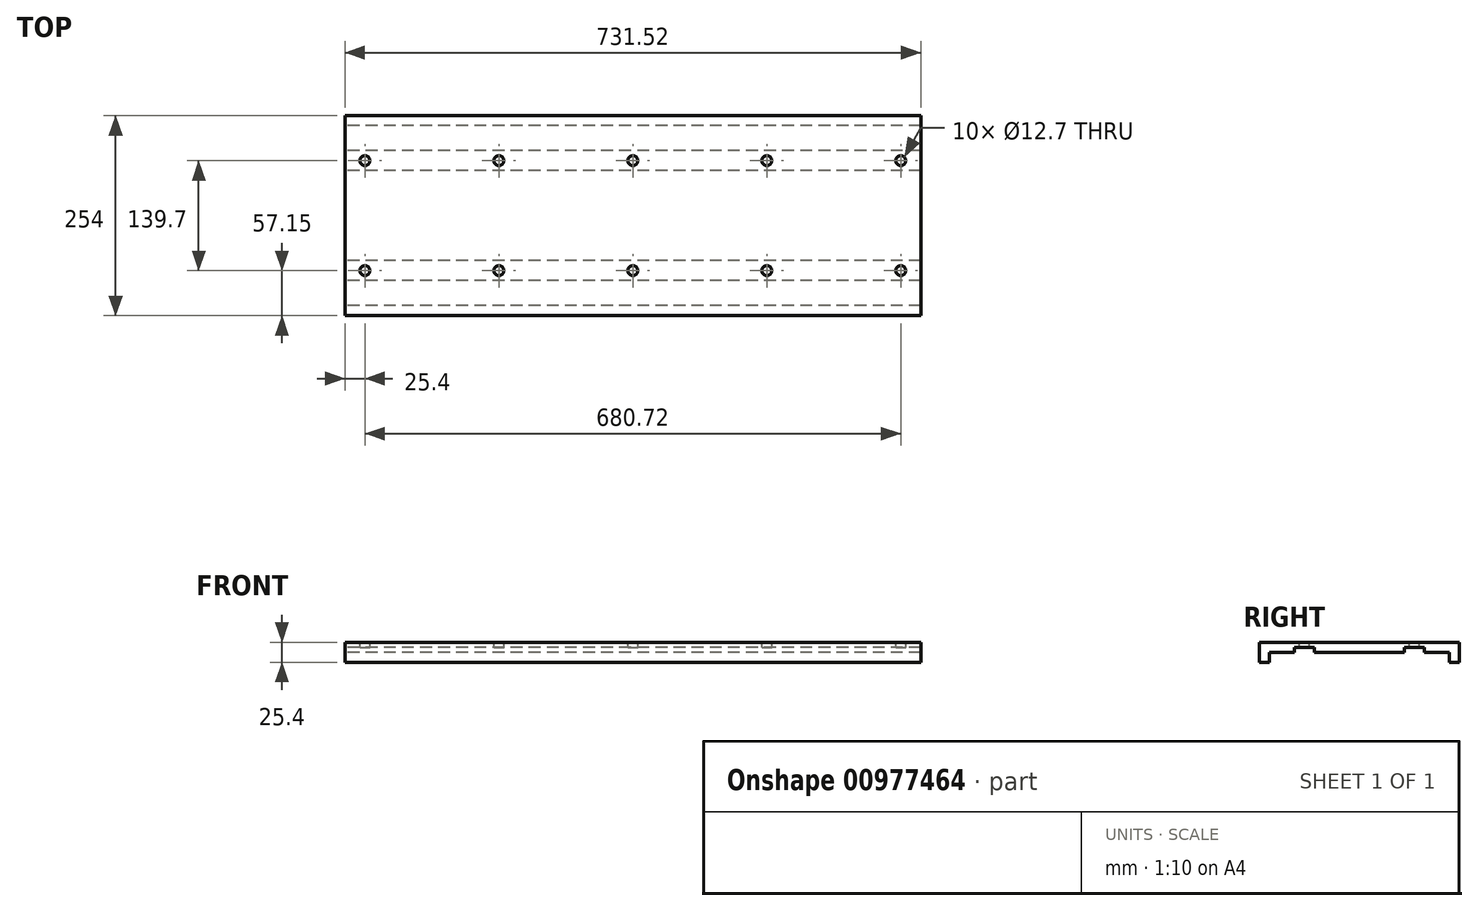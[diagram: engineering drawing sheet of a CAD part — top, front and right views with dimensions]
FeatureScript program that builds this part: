
annotation { "Feature Type Name" : "Feature", "Feature Type Description" : "" }
export const myFeature = defineFeature(function(context is Context, id is Id, definition is map)
    precondition{}
    {
        {
            var Q0;
            Q0=qCreatedBy(makeId("Right.planeOp"),FACE);
            var sketch = newSketch(context, id + "F0", { "sketchPlane" : qUnion([Q0])});
            skLineSegment(sketch, "E0.bottom", {"start": v(57.15, 6.35) * mm, "end": v(-57.15, 6.35) * mm});
            skLineSegment(sketch, "E0.top", {"start": v(57.15, -6.35) * mm, "end": v(-57.15, -6.35) * mm});
            skPoint(sketch, "E0.middle", {"position": v(0, 0) * mm});
            skLineSegment(sketch, "E1", {"start": v(-57.15, -6.35) * mm, "end": v(-57.15, 0) * mm});
            skLineSegment(sketch, "E2", {"start": v(-57.15, 0) * mm, "end": v(-82.55, 0) * mm});
            skLineSegment(sketch, "E3", {"start": v(-82.55, 0) * mm, "end": v(-82.55, -6.35) * mm});
            skLineSegment(sketch, "E4", {"start": v(-82.55, -6.35) * mm, "end": v(-114.3, -6.35) * mm});
            skLineSegment(sketch, "E5", {"start": v(-114.3, -6.35) * mm, "end": v(-114.3, -19.05) * mm});
            skLineSegment(sketch, "E6", {"start": v(-114.3, -19.05) * mm, "end": v(-127, -19.05) * mm});
            skLineSegment(sketch, "E7", {"start": v(-127, -19.05) * mm, "end": v(-127, 6.35) * mm});
            skLineSegment(sketch, "E8", {"start": v(-127, 6.35) * mm, "end": v(-57.15, 6.35) * mm});
            skLineSegment(sketch, "E9.MirrorCS", {"start": v(127, 6.35) * mm, "end": v(57.15, 6.35) * mm});
            skLineSegment(sketch, "E10.MirrorCS", {"start": v(127, -19.05) * mm, "end": v(127, 6.35) * mm});
            skLineSegment(sketch, "E11.MirrorCS", {"start": v(114.3, -19.05) * mm, "end": v(127, -19.05) * mm});
            skLineSegment(sketch, "E12.MirrorCS", {"start": v(82.55, -6.35) * mm, "end": v(114.3, -6.35) * mm});
            skLineSegment(sketch, "E13.MirrorCS", {"start": v(82.55, 0) * mm, "end": v(82.55, -6.35) * mm});
            skLineSegment(sketch, "E14.MirrorCS", {"start": v(57.15, 0) * mm, "end": v(82.55, 0) * mm});
            skLineSegment(sketch, "E15.MirrorCS", {"start": v(114.3, -6.35) * mm, "end": v(114.3, -19.05) * mm});
            skLineSegment(sketch, "E16.MirrorCS", {"start": v(57.15, -6.35) * mm, "end": v(57.15, 0) * mm});
            skSolve(sketch);
        }
        {
            var Q0;
            Q0=makeQuery(id+"F0.imprint","IMPRINT",FACE,{"disambiguationData":[TD([[makeQuery(id+"F0.imprint","IMPRINT",EDGE,{"derivedFrom":sQuery(id+"F0.wireOp",EDGE,"E0.bottom")}),1.0]])]});
            extrude(context, id + "F1", {"entities" : qUnion([Q0]), "endBound" : BoundingType.SYMMETRIC, "depth" : 731.52 * mm, "offsetDistance" : 25.4 * mm});
        }
        {
            var Q0;
            Q0=makeQuery(id+"F1.opExtrude","SWEPT_FACE",FACE,{"disambiguationData":[OSD([sQuery(id+"F0.wireOp",EDGE,"E0.bottom"),sQuery(id+"F0.wireOp",EDGE,"E8"),sQuery(id+"F0.wireOp",EDGE,"E9.MirrorCS")])]});
            var sketch = newSketch(context, id + "F2", { "sketchPlane" : qUnion([Q0])});
            skCircle(sketch, "E17", {"center": v(0, -69.85) * mm, "radius": 6.35 * mm});
            skCircle(sketch, "E18", {"center": v(170.18, -69.85) * mm, "radius": 6.35 * mm});
            skCircle(sketch, "E19", {"center": v(340.36, -69.85) * mm, "radius": 6.35 * mm});
            skCircle(sketch, "E20.MirrorC", {"center": v(-170.18, -69.85) * mm, "radius": 6.35 * mm});
            skCircle(sketch, "E21.MirrorC", {"center": v(-340.36, -69.85) * mm, "radius": 6.35 * mm});
            skCircle(sketch, "E22.MirrorC", {"center": v(-340.36, 69.85) * mm, "radius": 6.35 * mm});
            skCircle(sketch, "E23.MirrorC", {"center": v(-170.18, 69.85) * mm, "radius": 6.35 * mm});
            skCircle(sketch, "E24.MirrorC", {"center": v(0, 69.85) * mm, "radius": 6.35 * mm});
            skCircle(sketch, "E25.MirrorC", {"center": v(170.18, 69.85) * mm, "radius": 6.35 * mm});
            skCircle(sketch, "E26.MirrorC", {"center": v(340.36, 69.85) * mm, "radius": 6.35 * mm});
            skSolve(sketch);
        }
        {
            var Q0;
            Q0 = qSketchRegion(id + "F2", true);
            extrude(context, id + "F3", {"entities" : qUnion([Q0]), "operationType" : NewBodyOperationType.REMOVE, "oppositeDirection" : true, "depth" : 12.7 * mm, "offsetDistance" : 25.4 * mm});
        }
    });
